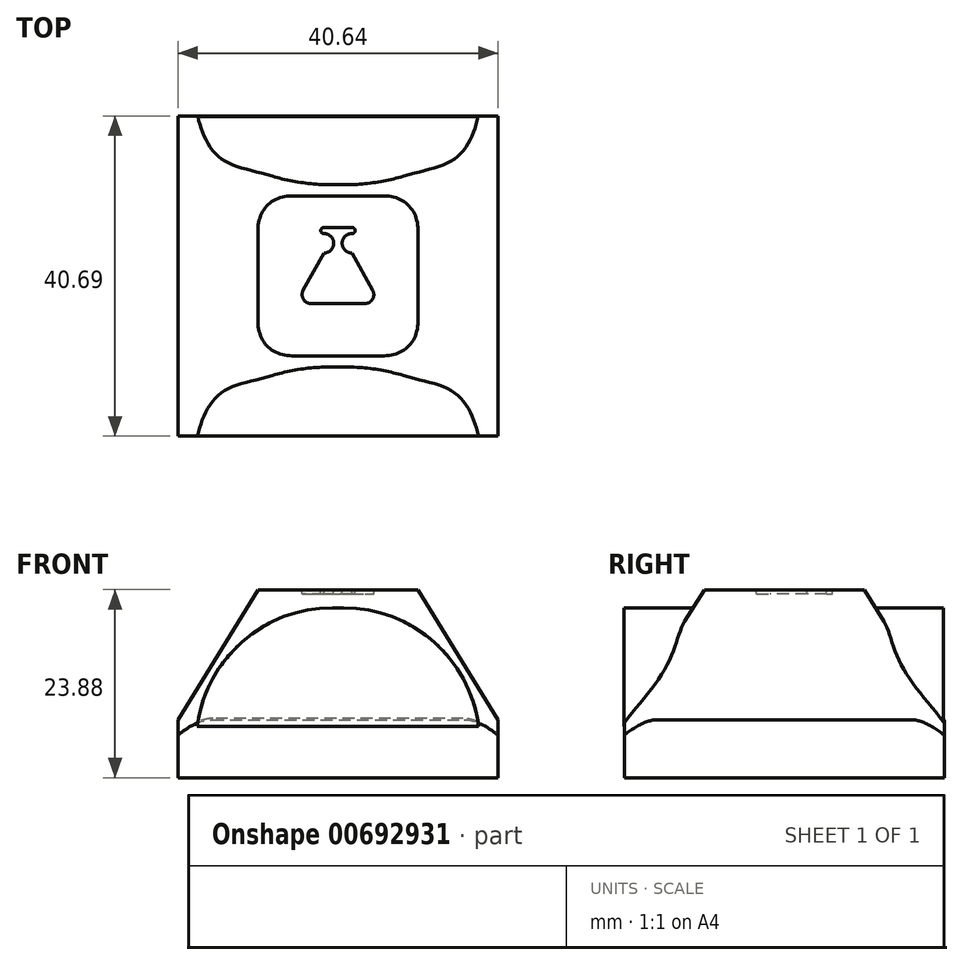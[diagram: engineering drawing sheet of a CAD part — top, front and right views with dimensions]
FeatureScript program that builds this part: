
annotation { "Feature Type Name" : "Feature", "Feature Type Description" : "" }
export const myFeature = defineFeature(function(context is Context, id is Id, definition is map)
    precondition{}
    {
        {
            var Q0;
            Q0=qCreatedBy(makeId("Top.planeOp"),FACE);
            var sketch = newSketch(context, id + "F0", { "sketchPlane" : qUnion([Q0])});
            skLineSegment(sketch, "E0.bottom", {"start": v(-40.64, 35.15) * mm, "end": v(0, 35.15) * mm});
            skLineSegment(sketch, "E0.top", {"start": v(-40.64, -5.49) * mm, "end": v(0, -5.49) * mm});
            skLineSegment(sketch, "E0.left", {"start": v(-40.64, 35.15) * mm, "end": v(-40.64, -5.49) * mm});
            skLineSegment(sketch, "E0.right", {"start": v(0, 35.15) * mm, "end": v(0, -5.49) * mm});
            skSolve(sketch);
        }
        {
            var Q0;
            Q0=makeQuery(id+"F0.imprint","IMPRINT",FACE,{"disambiguationData":[TD([[makeQuery(id+"F0.imprint","IMPRINT",EDGE,{"derivedFrom":sQuery(id+"F0.wireOp",EDGE,"E0.bottom")}),-1.0]])]});
            extrude(context, id + "F1", {"entities" : qUnion([Q0]), "depth" : 23.88 * mm, "offsetDistance" : 25.4 * mm});
        }
        {
            var Q0;
            Q0=makeQuery(id+"F1.opExtrude","CAP_FACE",FACE,{"disambiguationData":[OSD([sQuery(id+"F0.wireOp",EDGE,"E0.bottom"),sQuery(id+"F0.wireOp",EDGE,"E0.top"),sQuery(id+"F0.wireOp",EDGE,"E0.left"),sQuery(id+"F0.wireOp",EDGE,"E0.right")])],"isStart":false});
            chamfer(context, id + "F2", {"entities" : qUnion([Q0]), "chamferType" : ChamferType.TWO_OFFSETS, "width1" : 16.5 * mm, "oppositeDirection" : false, "width2" : 10.16 * mm, "tangentPropagation" : true});
        }
        {
            var Q0;
            Q0=qCreatedBy(makeId("Front.planeOp"),FACE);
            var sketch = newSketch(context, id + "F3", { "sketchPlane" : qUnion([Q0])});
            skArc(sketch, "E1.0", {"start": v(-21.02, 21.59) * mm, "mid": v(-32.44, 17.3) * mm, "end": v(-38.2, 6.54) * mm});
            skLineSegment(sketch, "E1.1", {"start": v(-21.02, 21.59) * mm, "end": v(-19.62, 21.59) * mm});
            skArc(sketch, "E1.2", {"start": v(-19.62, 21.59) * mm, "mid": v(-8.2, 17.3) * mm, "end": v(-2.44, 6.54) * mm});
            skLineSegment(sketch, "E1.3", {"start": v(-2.44, 6.54) * mm, "end": v(-38.2, 6.54) * mm});
            skSolve(sketch);
        }
        {
            var Q0;
            Q0 = qSketchRegion(id + "F3", true);
            extrude(context, id + "F4", {"entities" : qUnion([Q0]), "operationType" : NewBodyOperationType.ADD, "depth" : 5.54 * mm, "offsetDistance" : 25.4 * mm, "hasSecondDirection" : true, "secondDirectionOppositeDirection" : true, "secondDirectionDepth" : 35.05 * mm});
        }
        {
            var Q0;
            Q0=makeQuery(id+"F1.opExtrude","CAP_FACE",FACE,{"disambiguationData":[OSD([sQuery(id+"F0.wireOp",EDGE,"E0.bottom"),sQuery(id+"F0.wireOp",EDGE,"E0.top"),sQuery(id+"F0.wireOp",EDGE,"E0.left"),sQuery(id+"F0.wireOp",EDGE,"E0.right")])],"isStart":false});
            var sketch = newSketch(context, id + "F5", { "sketchPlane" : qUnion([Q0])});
            skLineSegment(sketch, "E2", {"start": v(-20.32, 25) * mm, "end": v(-20.32, 4.67) * mm});
            skLineSegment(sketch, "E3", {"start": v(-20.32, 20.96) * mm, "end": v(-22.1, 20.96) * mm});
            skArc(sketch, "E4", {"start": v(-22.1, 20.96) * mm, "mid": v(-22.5, 20.6) * mm, "end": v(-22.12, 20.2) * mm});
            skArc(sketch, "E5", {"start": v(-22.1, 17.72) * mm, "mid": v(-20.86, 18.97) * mm, "end": v(-22.12, 20.2) * mm});
            skLineSegment(sketch, "E6", {"start": v(-23.74, 11.31) * mm, "end": v(-20.32, 11.31) * mm});
            skPoint(sketch, "E7.orphan", {"position": v(-20.32, 11.4) * mm});
            skArc(sketch, "E8.MirrorCS", {"start": v(-18.54, 20.96) * mm, "mid": v(-18.13, 20.6) * mm, "end": v(-18.52, 20.2) * mm});
            skLineSegment(sketch, "E9.MirrorCS", {"start": v(-16.9, 11.31) * mm, "end": v(-20.32, 11.31) * mm});
            skArc(sketch, "E10.MirrorCS", {"start": v(-18.54, 17.72) * mm, "mid": v(-19.78, 18.97) * mm, "end": v(-18.52, 20.2) * mm});
            skLineSegment(sketch, "E11.MirrorCS", {"start": v(-20.32, 20.96) * mm, "end": v(-18.54, 20.96) * mm});
            skArc(sketch, "E12", {"start": v(-24.73, 13) * mm, "mid": v(-24.72, 11.87) * mm, "end": v(-23.74, 11.31) * mm});
            skLineSegment(sketch, "E13", {"start": v(-22.1, 17.72) * mm, "end": v(-24.73, 13) * mm});
            skLineSegment(sketch, "E14.MirrorCS", {"start": v(-18.54, 17.72) * mm, "end": v(-15.9, 13) * mm});
            skArc(sketch, "E15.MirrorCS", {"start": v(-15.9, 13) * mm, "mid": v(-15.92, 11.87) * mm, "end": v(-16.9, 11.31) * mm});
            skSolve(sketch);
        }
        {
            var Q0;
            {var subQ0=sQuery(id+"F5.wireOp",EDGE,"E3");Q0=makeQuery(id+"F5.imprint","IMPRINT",FACE,{"disambiguationData":[TD([[makeQuery(id+"F5.imprint","IMPRINT",EDGE,{"derivedFrom":subQ0}),1.0]])]});}
            var Q1;
            {var subQ0=sQuery(id+"F5.wireOp",EDGE,"E9.MirrorCS");Q1=makeQuery(id+"F5.imprint","IMPRINT",FACE,{"disambiguationData":[TD([[makeQuery(id+"F5.imprint","IMPRINT",EDGE,{"derivedFrom":subQ0}),-1.0]])]});}
            extrude(context, id + "F6", {"entities" : qUnion([Q0, Q1]), "operationType" : NewBodyOperationType.REMOVE, "oppositeDirection" : true, "depth" : 0.5 * mm, "offsetDistance" : 25.4 * mm});
        }
        {
            var Q0;
            Q0=makeQuery(id+"F2.opChamfer","BLEND_EDGE",EDGE,{"blendedFrom":[makeQuery(id+"F1.opExtrude","CAP_EDGE",EDGE,{"disambiguationData":[OSD([sQuery(id+"F0.wireOp",EDGE,"E0.top")])],"isStart":false}),makeQuery(id+"F1.opExtrude","CAP_EDGE",EDGE,{"disambiguationData":[OSD([sQuery(id+"F0.wireOp",EDGE,"E0.left")])],"isStart":false})],"blendedInto":[]});
            var Q1;
            Q1=makeQuery(id+"F2.opChamfer","BLEND_EDGE",EDGE,{"blendedFrom":[makeQuery(id+"F1.opExtrude","CAP_EDGE",EDGE,{"disambiguationData":[OSD([sQuery(id+"F0.wireOp",EDGE,"E0.top")])],"isStart":false}),makeQuery(id+"F1.opExtrude","CAP_EDGE",EDGE,{"disambiguationData":[OSD([sQuery(id+"F0.wireOp",EDGE,"E0.right")])],"isStart":false})],"blendedInto":[]});
            var Q2;
            Q2=makeQuery(id+"F2.opChamfer","BLEND_EDGE",EDGE,{"blendedFrom":[makeQuery(id+"F1.opExtrude","CAP_EDGE",EDGE,{"disambiguationData":[OSD([sQuery(id+"F0.wireOp",EDGE,"E0.bottom")])],"isStart":false}),makeQuery(id+"F1.opExtrude","CAP_EDGE",EDGE,{"disambiguationData":[OSD([sQuery(id+"F0.wireOp",EDGE,"E0.right")])],"isStart":false})],"blendedInto":[]});
            var Q3;
            Q3=makeQuery(id+"F2.opChamfer","BLEND_EDGE",EDGE,{"blendedFrom":[makeQuery(id+"F1.opExtrude","CAP_EDGE",EDGE,{"disambiguationData":[OSD([sQuery(id+"F0.wireOp",EDGE,"E0.bottom")])],"isStart":false}),makeQuery(id+"F1.opExtrude","CAP_EDGE",EDGE,{"disambiguationData":[OSD([sQuery(id+"F0.wireOp",EDGE,"E0.left")])],"isStart":false})],"blendedInto":[]});
            fillet(context, id + "F7", {"entities" : qUnion([Q0, Q1, Q2, Q3]), "radius" : 5.08 * mm, "tangentPropagation" : true, "allowEdgeOverflow" : false});
        }
    });
